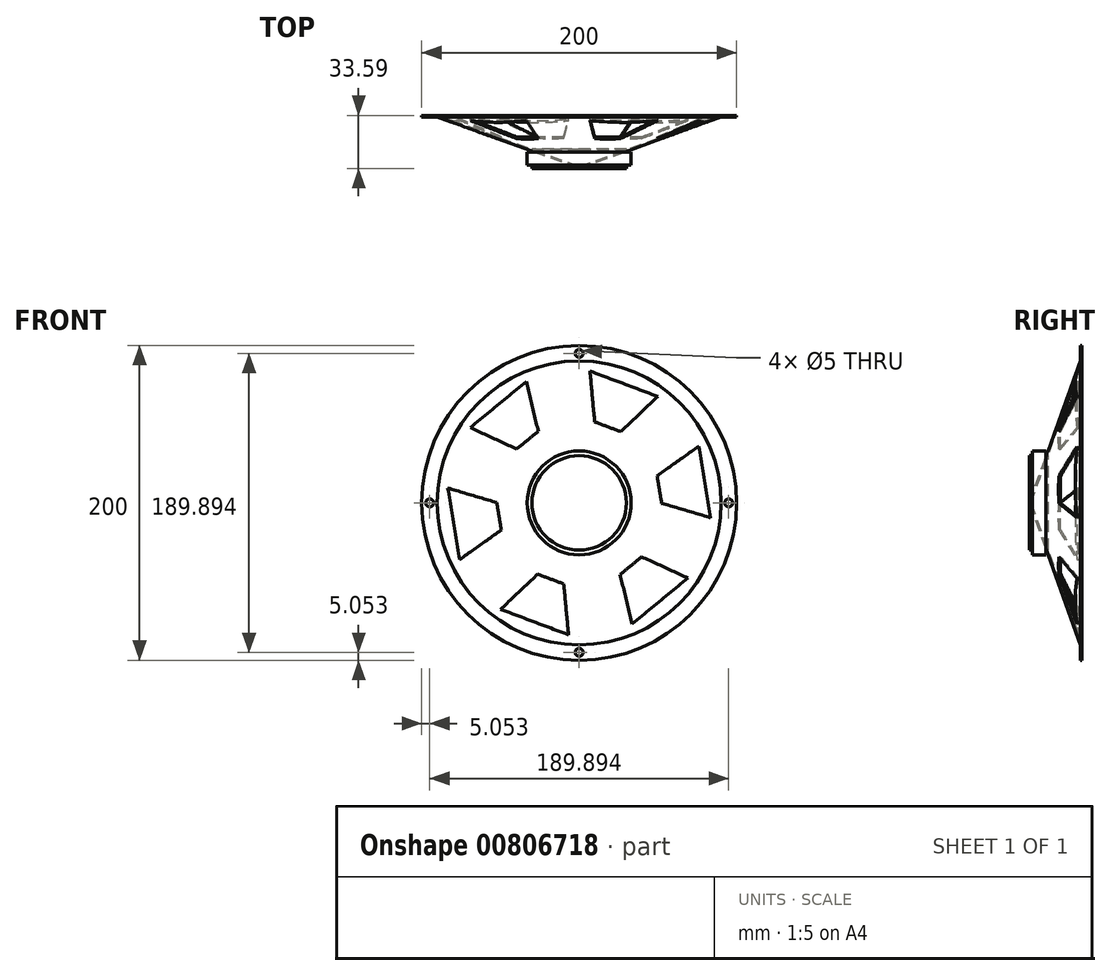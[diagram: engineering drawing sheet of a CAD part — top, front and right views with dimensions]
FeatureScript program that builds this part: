
annotation { "Feature Type Name" : "Feature", "Feature Type Description" : "" }
export const myFeature = defineFeature(function(context is Context, id is Id, definition is map)
    precondition{}
    {
        {
            var Q0;
            Q0=qCreatedBy(makeId("Right.planeOp"),FACE);
            var sketch = newSketch(context, id + "F0", { "sketchPlane" : qUnion([Q0])});
            skLineSegment(sketch, "E0.bottom", {"start": v(0, 0) * mm, "end": v(2.03, 0) * mm});
            skLineSegment(sketch, "E0.top", {"start": v(0, 30) * mm, "end": v(2.03, 30) * mm});
            skLineSegment(sketch, "E0.left", {"start": v(0, 0) * mm, "end": v(0, 30) * mm});
            skLineSegment(sketch, "E0.right", {"start": v(2.03, 0) * mm, "end": v(2.03, 30) * mm});
            skLineSegment(sketch, "E1.bottom", {"start": v(10.46, 0) * mm, "end": v(12.32, 0) * mm});
            skLineSegment(sketch, "E1.top", {"start": v(10.46, 30) * mm, "end": v(12.32, 30) * mm});
            skLineSegment(sketch, "E1.left", {"start": v(10.46, 0) * mm, "end": v(10.46, 30) * mm});
            skLineSegment(sketch, "E1.right", {"start": v(12.32, 0) * mm, "end": v(12.32, 30) * mm});
            skSolve(sketch);
        }
        {
            var Q0;
            Q0=qSketchRegion(id+"F0",true);
            var Q1;
            Q1=sQuery(id+"F0.wireOp",EDGE,"E0.bottom");
            revolve(context, id + "F1", {"surfaceOperationType" : NewSurfaceOperationType.NEW, "entities" : qUnion([Q0]), "axis" : qUnion([Q1]), "revolveType" : RevolveType.FULL});
        }
        {
            var Q0;
            Q0=qCreatedBy(makeId("Right.planeOp"),FACE);
            var sketch = newSketch(context, id + "F2", { "sketchPlane" : qUnion([Q0])});
            skLineSegment(sketch, "E2.bottom", {"start": v(2.03, 0) * mm, "end": v(10.46, 0) * mm});
            skLineSegment(sketch, "E2.top", {"start": v(2.03, 33) * mm, "end": v(10.46, 33) * mm});
            skLineSegment(sketch, "E2.left", {"start": v(2.03, 0) * mm, "end": v(2.03, 33) * mm});
            skLineSegment(sketch, "E2.right", {"start": v(10.46, 0) * mm, "end": v(10.46, 33) * mm});
            skSolve(sketch);
        }
        {
            var Q0;
            Q0=qSketchRegion(id+"F2",true);
            var Q1;
            Q1=sQuery(id+"F2.wireOp",EDGE,"E2.bottom");
            revolve(context, id + "F3", {"surfaceOperationType" : NewSurfaceOperationType.NEW, "entities" : qUnion([Q0]), "axis" : qUnion([Q1]), "revolveType" : RevolveType.FULL});
        }
        {
            var Q0;
            Q0=qCreatedBy(makeId("Right.planeOp"),FACE);
            var sketch = newSketch(context, id + "F4", { "sketchPlane" : qUnion([Q0])});
            skLineSegment(sketch, "E3", {"start": v(33.6, 90) * mm, "end": v(33.6, -90) * mm, "construction": true});
            skLineSegment(sketch, "E4", {"start": v(0, 0) * mm, "end": v(33.6, 0) * mm, "construction": true});
            skArc(sketch, "E5", {"start": v(12.32, 11.84) * mm, "mid": v(25.5, 50.23) * mm, "end": v(33.6, 90) * mm});
            skArc(sketch, "E6", {"start": v(18.64, 0) * mm, "mid": v(16.39, 6.4) * mm, "end": v(12.32, 11.84) * mm});
            skPoint(sketch, "E7.MirrorCS.end.orphan", {"position": v(33.6, -90) * mm});
            skPoint(sketch, "E8.orphan", {"position": v(12.32, -11.84) * mm});
            skSolve(sketch);
        }
        {
            var Q0;
            Q0=sQuery(id+"F4.wireOp",EDGE,"E5");
            var Q1;
            Q1=sQuery(id+"F4.wireOp",EDGE,"E6");
            var Q2;
            Q2=sQuery(id+"F4.wireOp",EDGE,"E4");
            revolve(context, id + "F5", {"bodyType" : ToolBodyType.SURFACE, "surfaceOperationType" : NewSurfaceOperationType.NEW, "surfaceEntities" : qUnion([Q0, Q1]), "axis" : qUnion([Q2]), "revolveType" : RevolveType.FULL});
        }
        {
            var Q0;
            Q0=qCreatedBy(makeId("Right.planeOp"),FACE);
            var sketch = newSketch(context, id + "F6", { "sketchPlane" : qUnion([Q0])});
            skLineSegment(sketch, "E9", {"start": v(1.06, 0) * mm, "end": v(33.6, 90) * mm});
            skLineSegment(sketch, "E10", {"start": v(33.6, 90) * mm, "end": v(33.6, 100) * mm});
            skLineSegment(sketch, "E11.0", {"start": v(32.6, 90.18) * mm, "end": v(32.6, 100) * mm});
            skLineSegment(sketch, "E11.1", {"start": v(0, 0) * mm, "end": v(32.6, 90.18) * mm});
            skLineSegment(sketch, "E12", {"start": v(0, 0) * mm, "end": v(1.06, 0) * mm});
            skLineSegment(sketch, "E13", {"start": v(32.6, 100) * mm, "end": v(33.6, 100) * mm});
            skLineSegment(sketch, "E14", {"start": v(0, 0) * mm, "end": v(94.96, 0) * mm, "construction": true});
            skSolve(sketch);
        }
        {
            var Q0;
            Q0=qSketchRegion(id+"F6",true);
            var Q1;
            Q1=sQuery(id+"F6.wireOp",EDGE,"E14");
            revolve(context, id + "F7", {"surfaceOperationType" : NewSurfaceOperationType.NEW, "entities" : qUnion([Q0]), "axis" : qUnion([Q1]), "revolveType" : RevolveType.FULL});
        }
        {
            var Q0;
            Q0=qCreatedBy(makeId("Front.planeOp"),FACE);
            var sketch = newSketch(context, id + "F8", { "sketchPlane" : qUnion([Q0])});
            skLineSegment(sketch, "E15", {"start": v(-69.12, 47.76) * mm, "end": v(-33.6, 77) * mm});
            skLineSegment(sketch, "E16", {"start": v(-33.6, 77) * mm, "end": v(-25.98, 45.5) * mm});
            skLineSegment(sketch, "E17", {"start": v(-25.98, 45.5) * mm, "end": v(-39.67, 34.24) * mm});
            skLineSegment(sketch, "E18", {"start": v(0, 0) * mm, "end": v(-32.83, 39.87) * mm, "construction": true});
            skLineSegment(sketch, "E19.MirrorCS", {"start": v(-69.12, 47.76) * mm, "end": v(-39.67, 34.24) * mm});
            skSolve(sketch);
        }
        {
            var Q0;
            Q0=qSketchRegion(id+"F8",true);
            extrude(context, id + "F9", {"entities" : qUnion([Q0]), "depth" : 135 * mm, "offsetDistance" : 25 * mm, "hasSecondDirection" : true, "secondDirectionOppositeDirection" : true, "secondDirectionDepth" : 304 * mm});
        }
        {
            var Q0;
            Q0=makeQuery(id+"F9.opExtrude","SWEPT_BODY",BODY,{"disambiguationData":[OSD([sQuery(id+"F8.wireOp",EDGE,"4yzcTzmE-Jsh7-dC9U-Scoi-qDLBZzaULgIm"),sQuery(id+"F8.wireOp",EDGE,"E15"),sQuery(id+"F8.wireOp",EDGE,"E16"),sQuery(id+"F8.wireOp",EDGE,"E17")])]});
            var Q1;
            Q1=sQuery(id+"F0.wireOp",EDGE,"E1.bottom");
            circularPattern(context, id + "F10", {"entities" : qUnion([Q0]), "axis" : qUnion([Q1]), "angle" : 360 * degree, "instanceCount" : 6, "equalSpace" : true});
        }
        {
            var Q0;
            Q0=makeQuery(id+"F10.opPattern","COPY",BODY,{"derivedFrom":makeQuery(id+"F9.opExtrude","SWEPT_BODY",BODY,{"disambiguationData":[OSD([sQuery(id+"F8.wireOp",EDGE,"4yzcTzmE-Jsh7-dC9U-Scoi-qDLBZzaULgIm"),sQuery(id+"F8.wireOp",EDGE,"E15"),sQuery(id+"F8.wireOp",EDGE,"E16"),sQuery(id+"F8.wireOp",EDGE,"E17")])]}),"instanceName":"1"});
            var Q1;
            Q1=makeQuery(id+"F9.opExtrude","SWEPT_BODY",BODY,{"disambiguationData":[OSD([sQuery(id+"F8.wireOp",EDGE,"4yzcTzmE-Jsh7-dC9U-Scoi-qDLBZzaULgIm"),sQuery(id+"F8.wireOp",EDGE,"E15"),sQuery(id+"F8.wireOp",EDGE,"E16"),sQuery(id+"F8.wireOp",EDGE,"E17")])]});
            var Q2;
            Q2=makeQuery(id+"F10.opPattern","COPY",BODY,{"derivedFrom":makeQuery(id+"F9.opExtrude","SWEPT_BODY",BODY,{"disambiguationData":[OSD([sQuery(id+"F8.wireOp",EDGE,"4yzcTzmE-Jsh7-dC9U-Scoi-qDLBZzaULgIm"),sQuery(id+"F8.wireOp",EDGE,"E15"),sQuery(id+"F8.wireOp",EDGE,"E16"),sQuery(id+"F8.wireOp",EDGE,"E17")])]}),"instanceName":"5"});
            var Q3;
            Q3=makeQuery(id+"F10.opPattern","COPY",BODY,{"derivedFrom":makeQuery(id+"F9.opExtrude","SWEPT_BODY",BODY,{"disambiguationData":[OSD([sQuery(id+"F8.wireOp",EDGE,"4yzcTzmE-Jsh7-dC9U-Scoi-qDLBZzaULgIm"),sQuery(id+"F8.wireOp",EDGE,"E15"),sQuery(id+"F8.wireOp",EDGE,"E16"),sQuery(id+"F8.wireOp",EDGE,"E17")])]}),"instanceName":"4"});
            var Q4;
            Q4=makeQuery(id+"F10.opPattern","COPY",BODY,{"derivedFrom":makeQuery(id+"F9.opExtrude","SWEPT_BODY",BODY,{"disambiguationData":[OSD([sQuery(id+"F8.wireOp",EDGE,"4yzcTzmE-Jsh7-dC9U-Scoi-qDLBZzaULgIm"),sQuery(id+"F8.wireOp",EDGE,"E15"),sQuery(id+"F8.wireOp",EDGE,"E16"),sQuery(id+"F8.wireOp",EDGE,"E17")])]}),"instanceName":"3"});
            var Q5;
            Q5=makeQuery(id+"F10.opPattern","COPY",BODY,{"derivedFrom":makeQuery(id+"F9.opExtrude","SWEPT_BODY",BODY,{"disambiguationData":[OSD([sQuery(id+"F8.wireOp",EDGE,"4yzcTzmE-Jsh7-dC9U-Scoi-qDLBZzaULgIm"),sQuery(id+"F8.wireOp",EDGE,"E15"),sQuery(id+"F8.wireOp",EDGE,"E16"),sQuery(id+"F8.wireOp",EDGE,"E17")])]}),"instanceName":"2"});
            var Q6;
            Q6=makeQuery(id+"F7.opRevolve","SWEPT_BODY",BODY,{"disambiguationData":[OSD([sQuery(id+"F6.wireOp",EDGE,"E9"),sQuery(id+"F6.wireOp",EDGE,"E10"),sQuery(id+"F6.wireOp",EDGE,"E11.0"),sQuery(id+"F6.wireOp",EDGE,"E11.1"),sQuery(id+"F6.wireOp",EDGE,"E12"),sQuery(id+"F6.wireOp",EDGE,"E13")])]});
            booleanBodies(context, id + "F11", {"operationType" : BooleanOperationType.SUBTRACTION, "tools" : qUnion([Q0, Q1, Q2, Q3, Q4, Q5]), "targets" : qUnion([Q6])});
        }
        {
            var Q0;
            Q0=makeQuery(id+"F7.opRevolve","SWEPT_FACE",FACE,{"disambiguationData":[OSD([sQuery(id+"F6.wireOp",EDGE,"E10")])]});
            var sketch = newSketch(context, id + "F12", { "sketchPlane" : qUnion([Q0])});
            skLineSegment(sketch, "E20", {"start": v(-100, 0) * mm, "end": v(100, 0) * mm, "construction": true});
            skLineSegment(sketch, "E21.bottom", {"start": v(90, 0) * mm, "end": v(99.9, 0) * mm, "construction": true});
            skLineSegment(sketch, "E21.top", {"start": v(90, 4.6) * mm, "end": v(99.9, 4.6) * mm, "construction": true});
            skLineSegment(sketch, "E21.left", {"start": v(90, 0) * mm, "end": v(90, 4.6) * mm, "construction": true});
            skLineSegment(sketch, "E21.right", {"start": v(99.9, 0) * mm, "end": v(99.9, 4.6) * mm, "construction": true});
            skCircle(sketch, "E22", {"center": v(94.95, 0) * mm, "radius": 2.5 * mm});
            skCircle(sketch, "E23.1.0", {"center": v(0, 94.95) * mm, "radius": 2.5 * mm});
            skCircle(sketch, "E23.2.0", {"center": v(-94.95, 0) * mm, "radius": 2.5 * mm});
            skCircle(sketch, "E23.3.0", {"center": v(0, -94.95) * mm, "radius": 2.5 * mm});
            skPoint(sketch, "E23.center", {"position": v(0, 0) * mm});
            skSolve(sketch);
        }
        {
            var Q0;
            Q0=makeQuery(id+"F12.imprint","IMPRINT",FACE,{"disambiguationData":[TD([[makeQuery(id+"F12.imprint","IMPRINT",EDGE,{"derivedFrom":sQuery(id+"F12.wireOp",EDGE,"E22")}),1.0]])]});
            var Q1;
            Q1=makeQuery(id+"F12.imprint","IMPRINT",FACE,{"disambiguationData":[TD([[makeQuery(id+"F12.imprint","IMPRINT",EDGE,{"derivedFrom":sQuery(id+"F12.wireOp",EDGE,"E23.2.0")}),1.0]])]});
            var Q2;
            Q2=makeQuery(id+"F12.imprint","IMPRINT",FACE,{"disambiguationData":[TD([[makeQuery(id+"F12.imprint","IMPRINT",EDGE,{"derivedFrom":sQuery(id+"F12.wireOp",EDGE,"E23.3.0")}),1.0]])]});
            var Q3;
            Q3=makeQuery(id+"F12.imprint","IMPRINT",FACE,{"disambiguationData":[TD([[makeQuery(id+"F12.imprint","IMPRINT",EDGE,{"derivedFrom":sQuery(id+"F12.wireOp",EDGE,"E23.1.0")}),1.0]])]});
            extrude(context, id + "F13", {"entities" : qUnion([Q0, Q1, Q2, Q3]), "operationType" : NewBodyOperationType.REMOVE, "endBound" : BoundingType.THROUGH_ALL, "oppositeDirection" : true, "depth" : 25 * mm, "offsetDistance" : 25 * mm});
        }
    });
